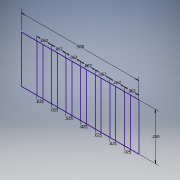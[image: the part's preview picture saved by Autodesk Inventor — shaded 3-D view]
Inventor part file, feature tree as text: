
AUTODESK INVENTOR PART (.ipt)
format: ipt  version: 2018 (Build 220112000, 112)  size: 112,128 bytes
history: native  units: in
note: dims shown in document units (in); Inventor stores cm internally (conversion verified against a paired STEP export)
features: sketch x1
ambient origin geometry x8: Origin, YZ Plane, XZ Plane, XY Plane, X Axis, Y Axis, Z Axis, Center Point
feature tree (1):
  sketch  "Sketch1"  dims[d0=0.5in d1=0.2in d2=0.062in d3=0.062in d4=0.062in d5=0.062in d6=0.062in d7=0.062in d8=0.062in d9=0.025in d10=0.025in d11=0.025in d12=0.025in d13=0.025in d14=0.025in d15=0.025in]
